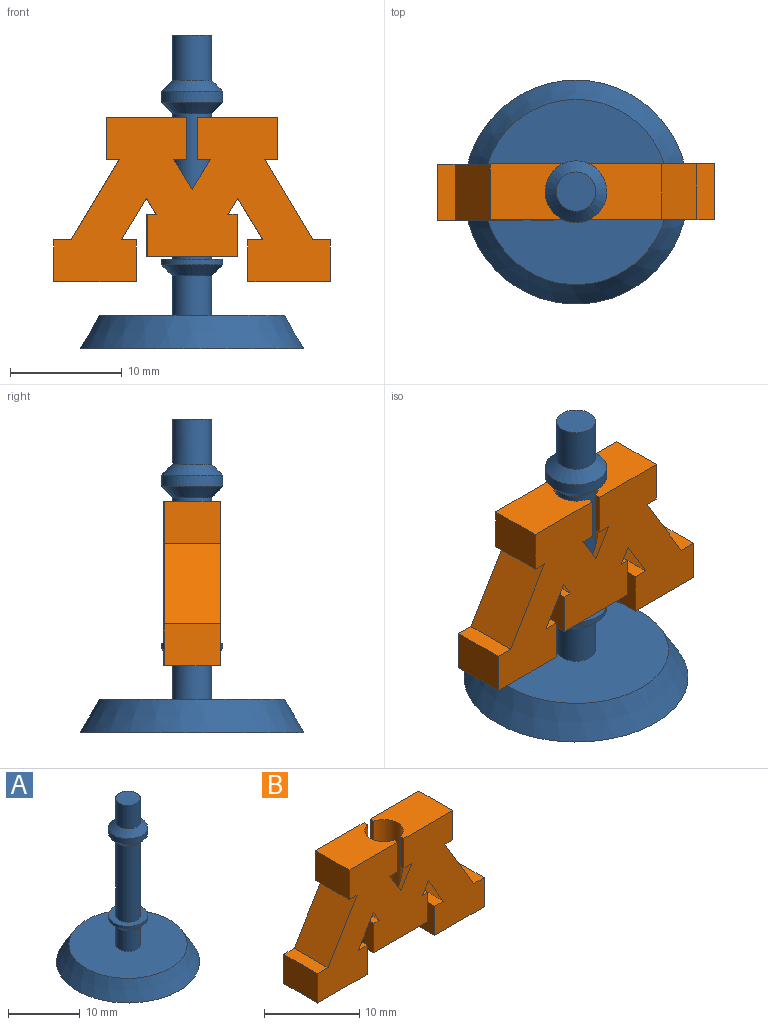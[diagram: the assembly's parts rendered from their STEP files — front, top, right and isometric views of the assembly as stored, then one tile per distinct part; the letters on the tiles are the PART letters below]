
ASSEMBLY  parts=2 mates=1
PART A: 13 faces, bbox 20x20x28 mm
  f0: cylinder r=1.75mm len=13mm, axis (0,0,-1), area 142.9mm2, adj f7,f8
  f1: cylinder r=1.75mm len=3.5mm, axis (0,0,-1), area 38.5mm2, adj f4,f5
  f2: cone r=10mm half-angle=30deg, axis (0,0,-1), area 198.8mm2, adj f3,f4
  f3: plane 20x20mm, normal (0,0,-1), area 314.2mm2, adj f2
  f4: plane 16.54x16.54mm, normal (0,0,1), area 205.1mm2, adj f1,f2
  f5: cone r=1.75mm half-angle=45deg, axis (0,0,1), area 20mm2, adj f1,f6
  f6: cylinder r=2.75mm len=5.5mm, axis (0,0,-1), area 8.6mm2, adj f5,f7
  f7: plane 5.5x5.5mm, normal (0,0,1), area 14.1mm2, adj f0,f6
  f8: cone r=1.75mm half-angle=45deg, axis (0,0,1), area 20mm2, adj f0,f9
  f9: cylinder r=2.75mm len=5.5mm, axis (0,0,-1), area 17.3mm2, adj f8,f10
  f10: cone r=2.75mm half-angle=45deg, axis (0,0,-1), area 20mm2, adj f9,f12
  f11: plane 3.5x3.5mm, normal (0,0,1), area 9.6mm2, adj f12
  f12: cylinder r=1.75mm len=4mm, axis (0,0,-1), area 44mm2, adj f10,f11
PART B: 42 faces, bbox 24.7x5x14.7 mm
  f0: plane 7.2x5mm, normal (0,0,1), area 31.5mm2, adj f1,f27,f28,f39,f40,f41
  f1: plane 3.78x0.55mm, normal (-1,0,0), area 2.1mm2, adj f0,f2,f40,f41
  f2: plane 1.35x1.18mm, normal (0,0,-1), area 1mm2, adj f1,f30,f40,f41
  f3: plane 2.71x1.63mm, normal (-0.86,0,0.52), area 2.4mm2, adj f4,f29,f39,f41
  f4: plane 2.71x1.63mm, normal (0.86,0,0.52), area 2.4mm2, adj f3,f32,f39,f41
  f5: plane 1.35x1.18mm, normal (0,0,-1), area 1mm2, adj f6,f31,f40,f41
  f6: plane 3.78x0.55mm, normal (1,0,0), area 2.1mm2, adj f5,f34,f40,f41
  f7: plane 5x3.74mm, normal (-1,0,0), area 18.7mm2, adj f8,f38,f39,f40
  f8: plane 7.36x5mm, normal (0,0,-1), area 36.8mm2, adj f7,f9,f39,f40
  f9: plane 5x3.74mm, normal (1,0,0), area 18.7mm2, adj f8,f10,f39,f40
  f10: plane 5x1.32mm, normal (0,0,1), area 6.6mm2, adj f9,f11,f39,f40
  f11: plane 5x3.73mm, normal (0.86,0,-0.51), area 21.7mm2, adj f10,f12,f39,f40
  f12: plane 5x1.43mm, normal (-0.85,0,-0.52), area 8.4mm2, adj f11,f13,f39,f40
  f13: plane 5x0.82mm, normal (0,0,1), area 4.1mm2, adj f12,f14,f39,f40
  f14: plane 5x3.76mm, normal (-1,0,0), area 18.8mm2, adj f13,f15,f39,f40
  f15: plane 8.04x5mm, normal (0,0,-1), area 27.6mm2, adj f14,f16,f39,f40,f41
  f16: plane 5x3.76mm, normal (1,0,0), area 18.8mm2, adj f15,f17,f39,f40
  f17: plane 5x0.82mm, normal (0,0,1), area 4.1mm2, adj f16,f18,f39,f40
  f18: plane 5x1.43mm, normal (0.85,0,-0.52), area 8.4mm2, adj f17,f19,f39,f40
  f19: plane 5x3.73mm, normal (-0.86,0,-0.51), area 21.7mm2, adj f18,f20,f39,f40
  f20: plane 5x1.32mm, normal (0,0,1), area 6.6mm2, adj f19,f21,f39,f40
  f21: plane 5x3.74mm, normal (-1,0,0), area 18.7mm2, adj f20,f22,f39,f40
  f22: plane 7.36x5mm, normal (0,0,-1), area 36.8mm2, adj f21,f23,f39,f40
  f23: plane 5x3.74mm, normal (1,0,0), area 18.7mm2, adj f22,f24,f39,f40
  f24: plane 5x1.55mm, normal (0,0,1), area 7.8mm2, adj f23,f25,f39,f40
  f25: plane 7.18x5mm, normal (0.86,0,0.51), area 41.8mm2, adj f24,f26,f39,f40
  f26: plane 5x1.16mm, normal (0,0,-1), area 5.8mm2, adj f25,f27,f39,f40
  f27: plane 5x3.78mm, normal (1,0,0), area 18.9mm2, adj f0,f26,f39,f40
  f28: plane 3.78x0.55mm, normal (-1,0,0), area 2.1mm2, adj f0,f29,f39,f41
  f29: plane 1.35x1.18mm, normal (0,0,-1), area 1mm2, adj f3,f28,f39,f41
  f30: plane 2.71x1.63mm, normal (-0.86,0,0.52), area 2.4mm2, adj f2,f31,f40,f41
  f31: plane 2.71x1.63mm, normal (0.86,0,0.52), area 2.4mm2, adj f5,f30,f40,f41
  f32: plane 1.35x1.18mm, normal (0,0,-1), area 1mm2, adj f4,f33,f39,f41
  f33: plane 3.78x0.55mm, normal (1,0,0), area 2.1mm2, adj f32,f34,f39,f41
  f34: plane 7.2x5mm, normal (0,0,1), area 31.5mm2, adj f6,f33,f35,f39,f40,f41
  f35: plane 5x3.78mm, normal (-1,0,0), area 18.9mm2, adj f34,f36,f39,f40
  f36: plane 5x1.16mm, normal (0,0,-1), area 5.8mm2, adj f35,f37,f39,f40
  f37: plane 7.18x5mm, normal (-0.86,0,0.51), area 41.8mm2, adj f36,f38,f39,f40
  f38: plane 5x1.55mm, normal (0,0,1), area 7.8mm2, adj f7,f37,f39,f40
  f39: plane 24.7x14.7mm, normal (0,-1,0), area 231.2mm2, adj f0,f3,f4,f7,f8,f9,f10,f11
  f40: plane 24.7x14.7mm, normal (0,1,0), area 231.2mm2, adj f0,f1,f2,f5,f6,f7,f8,f9
  f41: cylinder r=2mm len=12.43mm, axis (0,0,1), area 139.7mm2, adj f0,f1,f2,f3,f4,f5,f6,f15
PLACE A rot(axis=(0,0,1),90deg) t=(0,0,0)mm
PLACE B rot(axis=(0,0,1),0.1deg) t=(-0.01,2.5,5.83)mm
MATE cylindrical B.f41 <-> A.f0  axis (0,0,1) through (0,0,8.26)mm
